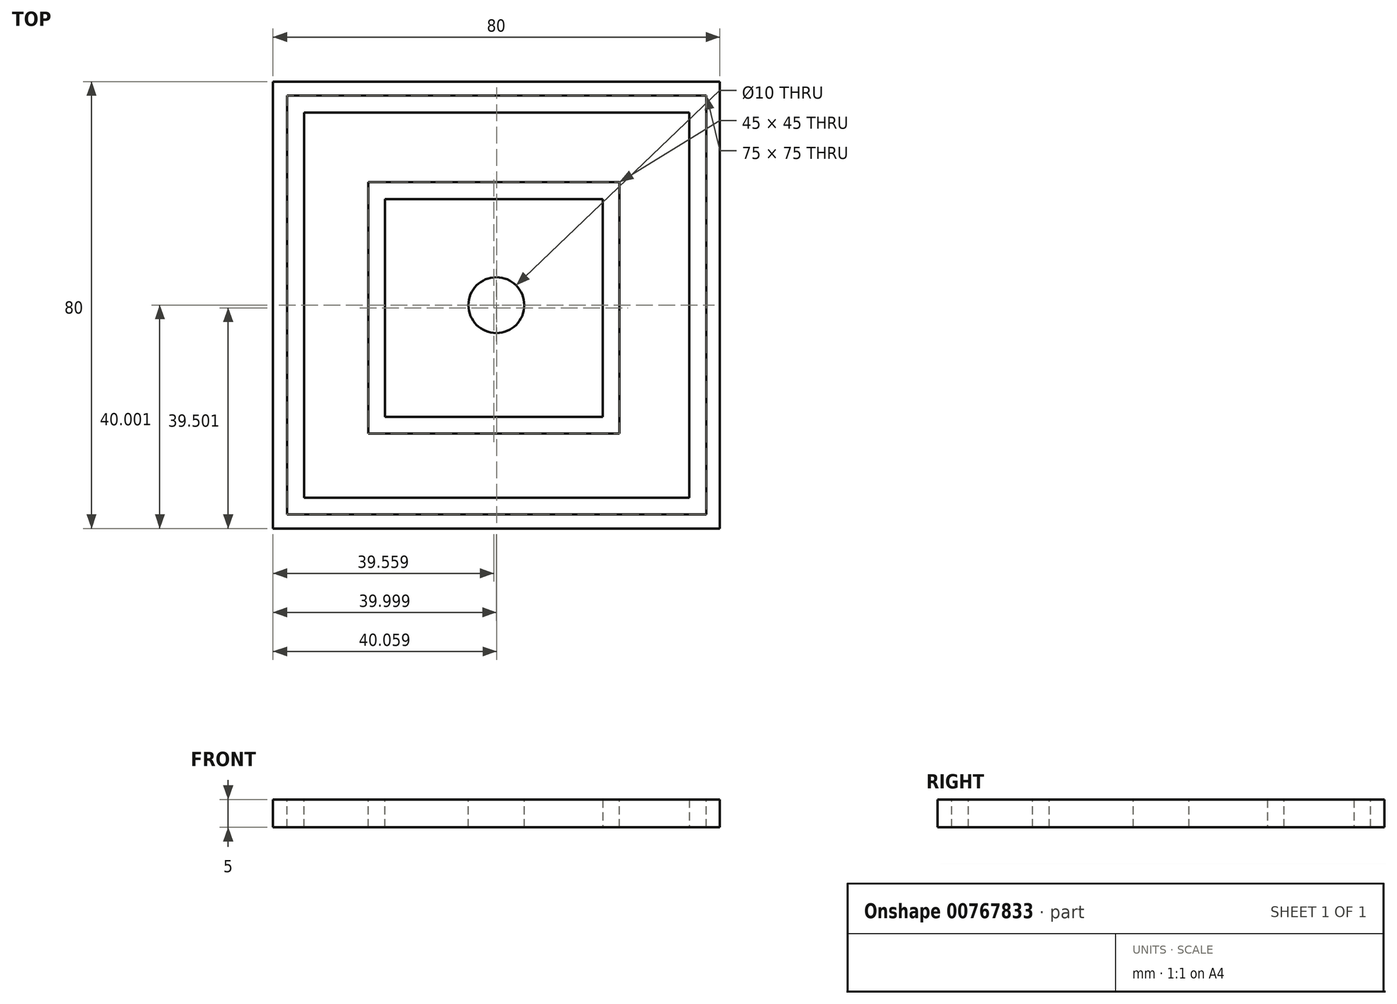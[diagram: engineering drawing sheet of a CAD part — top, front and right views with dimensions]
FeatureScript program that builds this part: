
annotation { "Feature Type Name" : "Feature", "Feature Type Description" : "" }
export const myFeature = defineFeature(function(context is Context, id is Id, definition is map)
    precondition{}
    {
        {
            var Q0;
            Q0=qCreatedBy(makeId("Top.planeOp"),FACE);
            var sketch = newSketch(context, id + "F0", { "sketchPlane" : qUnion([Q0])});
            skLineSegment(sketch, "E0.bottom", {"start": v(-16.2, 51.43) * mm, "end": v(63.8, 51.43) * mm});
            skLineSegment(sketch, "E0.top", {"start": v(-16.2, -28.57) * mm, "end": v(63.8, -28.57) * mm});
            skLineSegment(sketch, "E0.left", {"start": v(-16.2, 51.43) * mm, "end": v(-16.2, -28.57) * mm});
            skLineSegment(sketch, "E0.right", {"start": v(63.8, 51.43) * mm, "end": v(63.8, -28.57) * mm});
            skSolve(sketch);
        }
        {
            var Q0;
            Q0 = qSketchRegion(id + "F0", true);
            extrude(context, id + "F1", {"entities" : qUnion([Q0]), "depth" : 5 * mm, "offsetDistance" : 25 * mm});
        }
        {
            var Q0;
            Q0=makeQuery(id+"F1.opExtrude","CAP_FACE",FACE,{"disambiguationData":[OSD([sQuery(id+"F0.wireOp",EDGE,"E0.bottom"),sQuery(id+"F0.wireOp",EDGE,"E0.top"),sQuery(id+"F0.wireOp",EDGE,"E0.left"),sQuery(id+"F0.wireOp",EDGE,"E0.right")])],"isStart":false});
            var sketch = newSketch(context, id + "F2", { "sketchPlane" : qUnion([Q0])});
            skCircle(sketch, "E1", {"center": v(23.8, 11.43) * mm, "radius": 5 * mm});
            skPoint(sketch, "E1.centerSnap0", {"position": v(63.8, 11.43) * mm});
            skPoint(sketch, "E1.centerSnap1", {"position": v(23.8, 51.43) * mm});
            skSolve(sketch);
        }
        {
            var Q0;
            Q0 = qSketchRegion(id + "F2", true);
            extrude(context, id + "F3", {"entities" : qUnion([Q0]), "operationType" : NewBodyOperationType.REMOVE, "oppositeDirection" : true, "depth" : 5 * mm, "offsetDistance" : 25 * mm});
        }
        {
            var Q0;
            Q0=makeQuery(id+"F1.opExtrude","CAP_FACE",FACE,{"disambiguationData":[OSD([sQuery(id+"F0.wireOp",EDGE,"E0.bottom"),sQuery(id+"F0.wireOp",EDGE,"E0.top"),sQuery(id+"F0.wireOp",EDGE,"E0.left"),sQuery(id+"F0.wireOp",EDGE,"E0.right")])],"isStart":false});
            var sketch = newSketch(context, id + "F4", { "sketchPlane" : qUnion([Q0])});
            skLineSegment(sketch, "E2.bottom", {"start": v(-13.64, 48.93) * mm, "end": v(61.36, 48.93) * mm});
            skLineSegment(sketch, "E2.top", {"start": v(-13.64, 45.93) * mm, "end": v(61.36, 45.93) * mm});
            skLineSegment(sketch, "E2.left", {"start": v(-13.64, 48.93) * mm, "end": v(-13.64, 45.93) * mm});
            skLineSegment(sketch, "E2.right", {"start": v(61.36, 48.93) * mm, "end": v(61.36, 45.93) * mm});
            skSolve(sketch);
        }
        {
            var Q0;
            Q0 = qSketchRegion(id + "F4", true);
            extrude(context, id + "F5", {"entities" : qUnion([Q0]), "operationType" : NewBodyOperationType.REMOVE, "oppositeDirection" : true, "depth" : 20 * mm, "offsetDistance" : 25 * mm});
        }
        {
            var Q0;
            Q0=makeQuery(id+"F1.opExtrude","CAP_FACE",FACE,{"disambiguationData":[OSD([sQuery(id+"F0.wireOp",EDGE,"E0.bottom"),sQuery(id+"F0.wireOp",EDGE,"E0.top"),sQuery(id+"F0.wireOp",EDGE,"E0.left"),sQuery(id+"F0.wireOp",EDGE,"E0.right")])],"isStart":false});
            var sketch = newSketch(context, id + "F6", { "sketchPlane" : qUnion([Q0])});
            skLineSegment(sketch, "E3.bottom", {"start": v(-13.64, 48.93) * mm, "end": v(-10.64, 48.93) * mm});
            skLineSegment(sketch, "E3.top", {"start": v(-13.64, -26.07) * mm, "end": v(-10.64, -26.07) * mm});
            skLineSegment(sketch, "E3.left", {"start": v(-13.64, 48.93) * mm, "end": v(-13.64, -26.07) * mm});
            skLineSegment(sketch, "E3.right", {"start": v(-10.64, 48.93) * mm, "end": v(-10.64, -26.07) * mm});
            skSolve(sketch);
        }
        {
            var Q0;
            Q0 = qSketchRegion(id + "F6", true);
            extrude(context, id + "F7", {"entities" : qUnion([Q0]), "operationType" : NewBodyOperationType.REMOVE, "oppositeDirection" : true, "depth" : 25 * mm, "offsetDistance" : 25 * mm});
        }
        {
            var Q0;
            Q0=makeQuery(id+"F1.opExtrude","CAP_FACE",FACE,{"disambiguationData":[OSD([sQuery(id+"F0.wireOp",EDGE,"E0.bottom"),sQuery(id+"F0.wireOp",EDGE,"E0.top"),sQuery(id+"F0.wireOp",EDGE,"E0.left"),sQuery(id+"F0.wireOp",EDGE,"E0.right")])],"isStart":false});
            var sketch = newSketch(context, id + "F8", { "sketchPlane" : qUnion([Q0])});
            skLineSegment(sketch, "E4.bottom", {"start": v(-13.64, -26.07) * mm, "end": v(61.36, -26.07) * mm});
            skLineSegment(sketch, "E4.top", {"start": v(-13.64, -23.07) * mm, "end": v(61.36, -23.07) * mm});
            skLineSegment(sketch, "E4.left", {"start": v(-13.64, -26.07) * mm, "end": v(-13.64, -23.07) * mm});
            skLineSegment(sketch, "E4.right", {"start": v(61.36, -26.07) * mm, "end": v(61.36, -23.07) * mm});
            skSolve(sketch);
        }
        {
            var Q0;
            Q0 = qSketchRegion(id + "F8", true);
            extrude(context, id + "F9", {"entities" : qUnion([Q0]), "operationType" : NewBodyOperationType.REMOVE, "oppositeDirection" : true, "depth" : 25 * mm, "offsetDistance" : 25 * mm});
        }
        {
            var Q0;
            Q0=makeQuery(id+"F1.opExtrude","CAP_FACE",FACE,{"disambiguationData":[OSD([sQuery(id+"F0.wireOp",EDGE,"E0.bottom"),sQuery(id+"F0.wireOp",EDGE,"E0.top"),sQuery(id+"F0.wireOp",EDGE,"E0.left"),sQuery(id+"F0.wireOp",EDGE,"E0.right")])],"isStart":false});
            var sketch = newSketch(context, id + "F10", { "sketchPlane" : qUnion([Q0])});
            skLineSegment(sketch, "E5.bottom", {"start": v(61.36, 48.93) * mm, "end": v(58.36, 48.93) * mm});
            skLineSegment(sketch, "E5.top", {"start": v(61.36, -26.07) * mm, "end": v(58.36, -26.07) * mm});
            skLineSegment(sketch, "E5.left", {"start": v(61.36, 48.93) * mm, "end": v(61.36, -26.07) * mm});
            skLineSegment(sketch, "E5.right", {"start": v(58.36, 48.93) * mm, "end": v(58.36, -26.07) * mm});
            skSolve(sketch);
        }
        {
            var Q0;
            Q0 = qSketchRegion(id + "F10", true);
            extrude(context, id + "F11", {"entities" : qUnion([Q0]), "operationType" : NewBodyOperationType.REMOVE, "oppositeDirection" : true, "depth" : 25 * mm, "offsetDistance" : 25 * mm});
        }
        {
            var Q0;
            Q0=makeQuery(id+"F11.boolean.opBoolean","SPLIT",FACE,{"disambiguationData":[TD([makeQuery(id+"F3.boolean.opBoolean","COPY",FACE,{"derivedFrom":makeQuery(id+"F3.opExtrude","SWEPT_FACE",FACE,{"disambiguationData":[OSD([sQuery(id+"F2.wireOp",EDGE,"E1")])]})})])],"derivedFrom":makeQuery(id+"F1.opExtrude","CAP_FACE",FACE,{"disambiguationData":[OSD([sQuery(id+"F0.wireOp",EDGE,"E0.bottom"),sQuery(id+"F0.wireOp",EDGE,"E0.top"),sQuery(id+"F0.wireOp",EDGE,"E0.left"),sQuery(id+"F0.wireOp",EDGE,"E0.right")])],"isStart":false})});
            var sketch = newSketch(context, id + "F12", { "sketchPlane" : qUnion([Q0])});
            skLineSegment(sketch, "E6.bottom", {"start": v(0.86, 33.43) * mm, "end": v(45.86, 33.43) * mm});
            skLineSegment(sketch, "E6.top", {"start": v(0.86, 30.43) * mm, "end": v(45.86, 30.43) * mm});
            skLineSegment(sketch, "E6.left", {"start": v(0.86, 33.43) * mm, "end": v(0.86, 30.43) * mm});
            skLineSegment(sketch, "E6.right", {"start": v(45.86, 33.43) * mm, "end": v(45.86, 30.43) * mm});
            skSolve(sketch);
        }
        {
            var Q0;
            Q0 = qSketchRegion(id + "F12", true);
            extrude(context, id + "F13", {"entities" : qUnion([Q0]), "operationType" : NewBodyOperationType.REMOVE, "oppositeDirection" : true, "depth" : 25 * mm, "offsetDistance" : 25 * mm});
        }
        {
            var Q0;
            Q0=makeQuery(id+"F11.boolean.opBoolean","SPLIT",FACE,{"disambiguationData":[TD([makeQuery(id+"F3.boolean.opBoolean","COPY",FACE,{"derivedFrom":makeQuery(id+"F3.opExtrude","SWEPT_FACE",FACE,{"disambiguationData":[OSD([sQuery(id+"F2.wireOp",EDGE,"E1")])]})})])],"derivedFrom":makeQuery(id+"F1.opExtrude","CAP_FACE",FACE,{"disambiguationData":[OSD([sQuery(id+"F0.wireOp",EDGE,"E0.bottom"),sQuery(id+"F0.wireOp",EDGE,"E0.top"),sQuery(id+"F0.wireOp",EDGE,"E0.left"),sQuery(id+"F0.wireOp",EDGE,"E0.right")])],"isStart":false})});
            var sketch = newSketch(context, id + "F14", { "sketchPlane" : qUnion([Q0])});
            skLineSegment(sketch, "E7.bottom", {"start": v(0.86, 33.43) * mm, "end": v(3.86, 33.43) * mm});
            skLineSegment(sketch, "E7.top", {"start": v(0.86, -11.57) * mm, "end": v(3.86, -11.57) * mm});
            skLineSegment(sketch, "E7.left", {"start": v(0.86, 33.43) * mm, "end": v(0.86, -11.57) * mm});
            skLineSegment(sketch, "E7.right", {"start": v(3.86, 33.43) * mm, "end": v(3.86, -11.57) * mm});
            skSolve(sketch);
        }
        {
            var Q0;
            Q0 = qSketchRegion(id + "F14", true);
            extrude(context, id + "F15", {"entities" : qUnion([Q0]), "operationType" : NewBodyOperationType.REMOVE, "oppositeDirection" : true, "depth" : 25 * mm, "offsetDistance" : 25 * mm});
        }
        {
            var Q0;
            Q0=makeQuery(id+"F11.boolean.opBoolean","SPLIT",FACE,{"disambiguationData":[TD([makeQuery(id+"F3.boolean.opBoolean","COPY",FACE,{"derivedFrom":makeQuery(id+"F3.opExtrude","SWEPT_FACE",FACE,{"disambiguationData":[OSD([sQuery(id+"F2.wireOp",EDGE,"E1")])]})})])],"derivedFrom":makeQuery(id+"F1.opExtrude","CAP_FACE",FACE,{"disambiguationData":[OSD([sQuery(id+"F0.wireOp",EDGE,"E0.bottom"),sQuery(id+"F0.wireOp",EDGE,"E0.top"),sQuery(id+"F0.wireOp",EDGE,"E0.left"),sQuery(id+"F0.wireOp",EDGE,"E0.right")])],"isStart":false})});
            var sketch = newSketch(context, id + "F16", { "sketchPlane" : qUnion([Q0])});
            skLineSegment(sketch, "E8.bottom", {"start": v(0.86, -11.57) * mm, "end": v(45.86, -11.57) * mm});
            skLineSegment(sketch, "E8.top", {"start": v(0.86, -8.57) * mm, "end": v(45.86, -8.57) * mm});
            skLineSegment(sketch, "E8.left", {"start": v(0.86, -11.57) * mm, "end": v(0.86, -8.57) * mm});
            skLineSegment(sketch, "E8.right", {"start": v(45.86, -11.57) * mm, "end": v(45.86, -8.57) * mm});
            skSolve(sketch);
        }
        {
            var Q0;
            Q0 = qSketchRegion(id + "F16", true);
            extrude(context, id + "F17", {"entities" : qUnion([Q0]), "operationType" : NewBodyOperationType.REMOVE, "oppositeDirection" : true, "depth" : 25 * mm, "offsetDistance" : 25 * mm});
        }
        {
            var Q0;
            Q0=makeQuery(id+"F11.boolean.opBoolean","SPLIT",FACE,{"disambiguationData":[TD([makeQuery(id+"F3.boolean.opBoolean","COPY",FACE,{"derivedFrom":makeQuery(id+"F3.opExtrude","SWEPT_FACE",FACE,{"disambiguationData":[OSD([sQuery(id+"F2.wireOp",EDGE,"E1")])]})})])],"derivedFrom":makeQuery(id+"F1.opExtrude","CAP_FACE",FACE,{"disambiguationData":[OSD([sQuery(id+"F0.wireOp",EDGE,"E0.bottom"),sQuery(id+"F0.wireOp",EDGE,"E0.top"),sQuery(id+"F0.wireOp",EDGE,"E0.left"),sQuery(id+"F0.wireOp",EDGE,"E0.right")])],"isStart":false})});
            var sketch = newSketch(context, id + "F18", { "sketchPlane" : qUnion([Q0])});
            skLineSegment(sketch, "E9.bottom", {"start": v(45.86, 33.43) * mm, "end": v(42.86, 33.43) * mm});
            skLineSegment(sketch, "E9.top", {"start": v(45.86, -11.57) * mm, "end": v(42.86, -11.57) * mm});
            skLineSegment(sketch, "E9.left", {"start": v(45.86, 33.43) * mm, "end": v(45.86, -11.57) * mm});
            skLineSegment(sketch, "E9.right", {"start": v(42.86, 33.43) * mm, "end": v(42.86, -11.57) * mm});
            skSolve(sketch);
        }
        {
            var Q0;
            Q0 = qSketchRegion(id + "F18", true);
            extrude(context, id + "F19", {"entities" : qUnion([Q0]), "operationType" : NewBodyOperationType.REMOVE, "oppositeDirection" : true, "depth" : 25 * mm, "offsetDistance" : 25 * mm});
        }
    });
